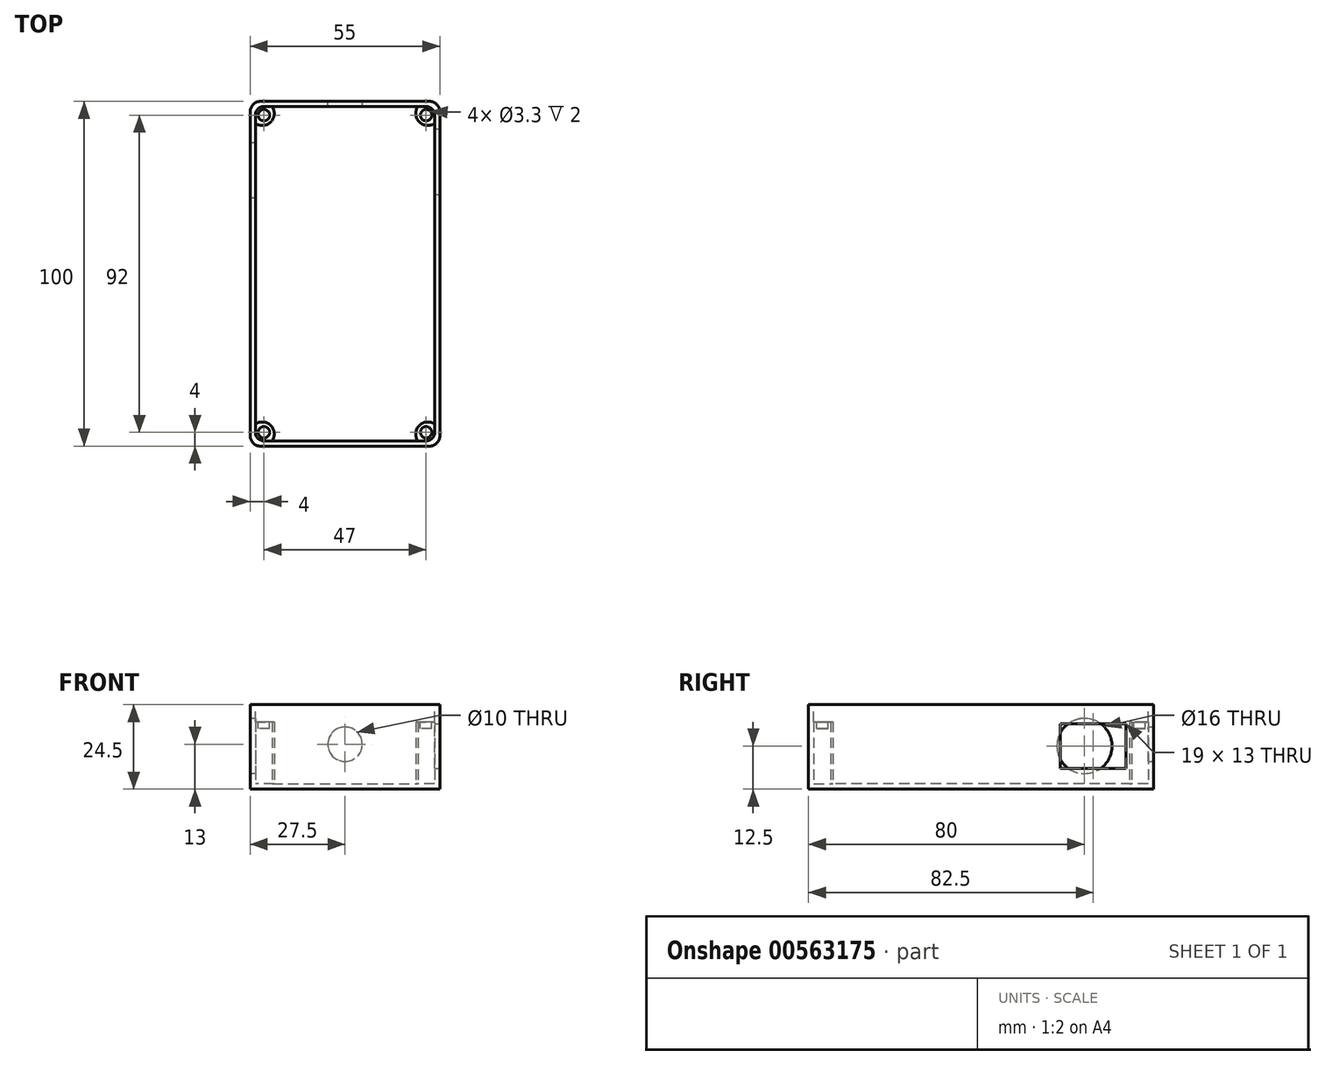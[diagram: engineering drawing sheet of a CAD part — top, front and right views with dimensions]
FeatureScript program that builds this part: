
annotation { "Feature Type Name" : "Feature", "Feature Type Description" : "" }
export const myFeature = defineFeature(function(context is Context, id is Id, definition is map)
    precondition{}
    {
        {
            var Q0;
            Q0=qCreatedBy(makeId("Top.planeOp"),FACE);
            var sketch = newSketch(context, id + "F0", { "sketchPlane" : qUnion([Q0])});
            skLineSegment(sketch, "E0.bottom", {"start": v(0, 0) * mm, "end": v(55, 0) * mm});
            skLineSegment(sketch, "E0.top", {"start": v(0, 100) * mm, "end": v(55, 100) * mm});
            skLineSegment(sketch, "E0.left", {"start": v(0, 0) * mm, "end": v(0, 100) * mm});
            skLineSegment(sketch, "E0.right", {"start": v(55, 0) * mm, "end": v(55, 100) * mm});
            skSolve(sketch);
        }
        {
            var Q0;
            Q0=makeQuery(id+"F0.imprint","IMPRINT",FACE,{"disambiguationData":[TD([[makeQuery(id+"F0.imprint","IMPRINT",EDGE,{"derivedFrom":sQuery(id+"F0.wireOp",EDGE,"E0.bottom")}),1.0]])]});
            extrude(context, id + "F1", {"entities" : qUnion([Q0]), "depth" : 24.5 * mm, "offsetDistance" : 25 * mm});
        }
        {
            var Q0;
            Q0=makeQuery(id+"F1.opExtrude","CAP_FACE",FACE,{"disambiguationData":[OSD([sQuery(id+"F0.wireOp",EDGE,"E0.bottom"),sQuery(id+"F0.wireOp",EDGE,"E0.top"),sQuery(id+"F0.wireOp",EDGE,"E0.left"),sQuery(id+"F0.wireOp",EDGE,"E0.right")])],"isStart":false});
            var sketch = newSketch(context, id + "F2", { "sketchPlane" : qUnion([Q0])});
            skLineSegment(sketch, "E1.bottom", {"start": v(1.5, 98.5) * mm, "end": v(53.5, 98.5) * mm});
            skLineSegment(sketch, "E1.top", {"start": v(1.5, 1.5) * mm, "end": v(53.5, 1.5) * mm});
            skLineSegment(sketch, "E1.left", {"start": v(1.5, 98.5) * mm, "end": v(1.5, 1.5) * mm});
            skLineSegment(sketch, "E1.right", {"start": v(53.5, 98.5) * mm, "end": v(53.5, 1.5) * mm});
            skLineSegment(sketch, "E2", {"start": v(27.5, 100) * mm, "end": v(27.5, 98.5) * mm});
            skPoint(sketch, "E2.endSnap0", {"position": v(27.5, 98.5) * mm});
            skLineSegment(sketch, "E3", {"start": v(0, 50) * mm, "end": v(1.5, 50) * mm});
            skLineSegment(sketch, "E4", {"start": v(27.5, 0) * mm, "end": v(27.5, 1.5) * mm});
            skLineSegment(sketch, "E5", {"start": v(55, 50) * mm, "end": v(53.5, 50) * mm});
            skSolve(sketch);
        }
        {
            var Q0;
            Q0 = qSketchRegion(id + "F2", true);
            extrude(context, id + "F3", {"entities" : qUnion([Q0]), "operationType" : NewBodyOperationType.REMOVE, "oppositeDirection" : true, "depth" : 23 * mm, "offsetDistance" : 25 * mm});
        }
        {
            var Q0;
            Q0=makeQuery(id+"F1.opExtrude","SWEPT_FACE",FACE,{"disambiguationData":[OSD([sQuery(id+"F0.wireOp",EDGE,"E0.top")])]});
            var sketch = newSketch(context, id + "F4", { "sketchPlane" : qUnion([Q0])});
            skCircle(sketch, "E6", {"center": v(-27.5, 13) * mm, "radius": 5 * mm});
            skLineSegment(sketch, "E7", {"start": v(-27.5, 24.5) * mm, "end": v(-27.5, 0) * mm, "construction": true});
            skSolve(sketch);
        }
        {
            var Q0;
            Q0 = qSketchRegion(id + "F4", true);
            extrude(context, id + "F5", {"entities" : qUnion([Q0]), "operationType" : NewBodyOperationType.REMOVE, "oppositeDirection" : true, "depth" : 2 * mm, "offsetDistance" : 25 * mm});
        }
        {
            var Q0;
            Q0=makeQuery(id+"F1.opExtrude","SWEPT_FACE",FACE,{"disambiguationData":[OSD([sQuery(id+"F0.wireOp",EDGE,"E0.left")])]});
            var sketch = newSketch(context, id + "F6", { "sketchPlane" : qUnion([Q0])});
            skCircle(sketch, "E8", {"center": v(-80, 12.5) * mm, "radius": 8 * mm});
            skSolve(sketch);
        }
        {
            var Q0;
            Q0 = qSketchRegion(id + "F6", true);
            extrude(context, id + "F7", {"entities" : qUnion([Q0]), "operationType" : NewBodyOperationType.REMOVE, "oppositeDirection" : true, "depth" : 2 * mm, "offsetDistance" : 25 * mm});
        }
        {
            var Q0;
            Q0=makeQuery(id+"F3.boolean.opBoolean","COPY",FACE,{"derivedFrom":makeQuery(id+"F3.opExtrude","CAP_FACE",FACE,{"disambiguationData":[OSD([sQuery(id+"F2.wireOp",EDGE,"E1.bottom"),sQuery(id+"F2.wireOp",EDGE,"E1.top"),sQuery(id+"F2.wireOp",EDGE,"E1.left"),sQuery(id+"F2.wireOp",EDGE,"E1.right")])],"isStart":false})});
            var sketch = newSketch(context, id + "F8", { "sketchPlane" : qUnion([Q0])});
            skCircle(sketch, "E9", {"center": v(3.5, 96.5) * mm, "radius": 3.5 * mm});
            skCircle(sketch, "E10", {"center": v(51.5, 96.5) * mm, "radius": 3.5 * mm});
            skCircle(sketch, "E11", {"center": v(51.5, 3.5) * mm, "radius": 3.5 * mm});
            skCircle(sketch, "E12", {"center": v(3.5, 3.5) * mm, "radius": 3.5 * mm});
            skSolve(sketch);
        }
        {
            var Q0;
            Q0 = qSketchRegion(id + "F8", true);
            extrude(context, id + "F9", {"entities" : qUnion([Q0]), "operationType" : NewBodyOperationType.ADD, "depth" : 18 * mm, "offsetDistance" : 25 * mm});
        }
        {
            var Q0;
            Q0=makeQuery(id+"F9.opExtrude","CAP_FACE",FACE,{"disambiguationData":[OSD([sQuery(id+"F8.wireOp",EDGE,"E9")])],"isStart":false});
            var sketch = newSketch(context, id + "F10", { "sketchPlane" : qUnion([Q0])});
            skCircle(sketch, "E13", {"center": v(4, 96) * mm, "radius": 1.65 * mm});
            skCircle(sketch, "E14.0.1.0", {"center": v(4, 4) * mm, "radius": 1.65 * mm});
            skCircle(sketch, "E14.1.0.0", {"center": v(51, 96) * mm, "radius": 1.65 * mm});
            skCircle(sketch, "E14.1.1.0", {"center": v(51, 4) * mm, "radius": 1.65 * mm});
            skLineSegment(sketch, "E14.direction1", {"start": v(4, 96) * mm, "end": v(51, 96) * mm, "construction": true});
            skLineSegment(sketch, "E14.direction2", {"start": v(4, 96) * mm, "end": v(4, 4) * mm, "construction": true});
            skSolve(sketch);
        }
        {
            var Q0;
            Q0 = qSketchRegion(id + "F10", true);
            extrude(context, id + "F11", {"entities" : qUnion([Q0]), "operationType" : NewBodyOperationType.REMOVE, "oppositeDirection" : true, "depth" : 2 * mm, "offsetDistance" : 25 * mm});
        }
        {
            var Q0;
            Q0=makeQuery(id+"F1.opExtrude","SWEPT_EDGE",EDGE,{"disambiguationData":[OSD([sQuery(id+"F0.wireOp",EDGE,"E0.top"),sQuery(id+"F0.wireOp",EDGE,"E0.left")])]});
            var Q1;
            Q1=makeQuery(id+"F1.opExtrude","SWEPT_EDGE",EDGE,{"disambiguationData":[OSD([sQuery(id+"F0.wireOp",EDGE,"E0.top"),sQuery(id+"F0.wireOp",EDGE,"E0.right")])]});
            var Q2;
            Q2=makeQuery(id+"F1.opExtrude","SWEPT_EDGE",EDGE,{"disambiguationData":[OSD([sQuery(id+"F0.wireOp",EDGE,"E0.bottom"),sQuery(id+"F0.wireOp",EDGE,"E0.left")])]});
            var Q3;
            Q3=makeQuery(id+"F1.opExtrude","SWEPT_EDGE",EDGE,{"disambiguationData":[OSD([sQuery(id+"F0.wireOp",EDGE,"E0.bottom"),sQuery(id+"F0.wireOp",EDGE,"E0.right")])]});
            fillet(context, id + "F12", {"entities" : qUnion([Q0, Q1, Q2, Q3]), "radius" : 3 * mm, "tangentPropagation" : true, "allowEdgeOverflow" : false});
        }
        {
            var Q0;
            Q0=makeQuery(id+"F3.boolean.opBoolean","COPY",EDGE,{"derivedFrom":makeQuery(id+"F3.opExtrude","SWEPT_EDGE",EDGE,{"disambiguationData":[OSD([sQuery(id+"F2.wireOp",EDGE,"E1.bottom"),sQuery(id+"F2.wireOp",EDGE,"E1.left")])]})});
            var Q1;
            Q1=makeQuery(id+"F3.boolean.opBoolean","COPY",EDGE,{"derivedFrom":makeQuery(id+"F3.opExtrude","SWEPT_EDGE",EDGE,{"disambiguationData":[OSD([sQuery(id+"F2.wireOp",EDGE,"E1.bottom"),sQuery(id+"F2.wireOp",EDGE,"E1.right")])]})});
            var Q2;
            Q2=makeQuery(id+"F3.boolean.opBoolean","COPY",EDGE,{"derivedFrom":makeQuery(id+"F3.opExtrude","SWEPT_EDGE",EDGE,{"disambiguationData":[OSD([sQuery(id+"F2.wireOp",EDGE,"E1.top"),sQuery(id+"F2.wireOp",EDGE,"E1.left")])]})});
            var Q3;
            Q3=makeQuery(id+"F3.boolean.opBoolean","COPY",EDGE,{"derivedFrom":makeQuery(id+"F3.opExtrude","SWEPT_EDGE",EDGE,{"disambiguationData":[OSD([sQuery(id+"F2.wireOp",EDGE,"E1.top"),sQuery(id+"F2.wireOp",EDGE,"E1.right")])]})});
            fillet(context, id + "F13", {"entities" : qUnion([Q0, Q1, Q2, Q3]), "radius" : 2.5 * mm, "tangentPropagation" : true, "allowEdgeOverflow" : false});
        }
        {
            var Q0;
            Q0=makeQuery(id+"F1.opExtrude","SWEPT_FACE",FACE,{"disambiguationData":[OSD([sQuery(id+"F0.wireOp",EDGE,"E0.right")])]});
            var sketch = newSketch(context, id + "F14", { "sketchPlane" : qUnion([Q0])});
            skLineSegment(sketch, "E15.bottom", {"start": v(73, 19) * mm, "end": v(92, 19) * mm});
            skLineSegment(sketch, "E15.top", {"start": v(73, 6) * mm, "end": v(92, 6) * mm});
            skLineSegment(sketch, "E15.left", {"start": v(73, 19) * mm, "end": v(73, 6) * mm});
            skLineSegment(sketch, "E15.right", {"start": v(92, 19) * mm, "end": v(92, 6) * mm});
            skSolve(sketch);
        }
        {
            var Q0;
            Q0 = qSketchRegion(id + "F14", true);
            extrude(context, id + "F15", {"entities" : qUnion([Q0]), "operationType" : NewBodyOperationType.REMOVE, "oppositeDirection" : true, "depth" : 2 * mm, "offsetDistance" : 25 * mm});
        }
    });
